# Revit family: Kombiventil 4006_M_SMART_SF_HF
name_source: partatom
category: Rohrzubehör
units: mm (PartAtom-declared; Revit-internal decimal feet)

## family parameters
Arbeitsebenenbasiert = Nein
Beim Laden mit Abzugskörper schneiden = Nein
Bemaßung runder Anschluss = Durchmesser verwenden
Gemeinsam genutzt = Nein
Immer vertikal = Ja
OmniClass-Nummer = 23.65.55.14
OmniClass-Titel = Valves for Liquid Services
Teiletyp = Unterbricht

## types (2) — shared parameters
Anwendungsgebiet = Das Kombiventil wird in allen pumpenbetriebenen Heiz- und Kühlanlagen eingesetzt.
Der Regler begrenzt automatisch den Volumenstrom im gewählten Anlagenteil auf den einmal eingestellten Wert, indem alle Druckschwankungen gemessen und ausgeregelt werden.
Somit sind keine Messungen erforderlich und die Regelung ist bei allen Betriebsbedingungen effektiv.
Das Kombiventil regelt den Volumenstrom der ventileigenen Voreinstellung auf einen konstanten Wert; die Membran regelt aufgrund des Druckes unmittelbar nach dem Regeleinsatz, sowie des Druckes davor.
Die Voreinstellung bezieht sich direkt auf den Volumenstrom; entsprechend kann die maximale Durchflussmenge bei der Montage direkt nach dem Diagramm eingestellt werden.
Somit sind z.B. Heizungsstränge, Kühlwasserkreisläufe, Deckenstrahlplatten, Kühldecken und Lufterhitzer ohne Rücksicht auf die Druckverteilung in der Anlage ohne weiteres abgleichbar.
Bauschutzkappe = Kunststoff
D03 = 19.5 mm  [stored 0.0639764 ft]
D04 = 25 mm  [stored 0.082021 ft]
D05 = 15 mm  [stored 0.0492126 ft]
D06 = 13.9 mm  [stored 0.0456037 ft]
Druckfeder = Federstahl
Gehäuse = DZR Messing CC770S
H01 = 37 mm  [stored 0.121391 ft]
H02 = 57.1 mm  [stored 0.187336 ft]
H03 = 20.5 mm  [stored 0.0672572 ft]
H04 = 9 mm  [stored 0.0295276 ft]
H05 = 5 mm  [stored 0.0164042 ft]
H06 = 48.5 mm
Hersteller = HERZ Armaturen Ges.m.b.H.
Hub = 4 mm
Impulsleitung = Kupfer Cu-DHP (CW024A)
KD01 = 17.55 mm  [stored 0.0575787 ft]
KD02 = 22 mm  [stored 0.0721785 ft]
KH01 = 10.8 mm  [stored 0.0354331 ft]
KH02 = 23 mm  [stored 0.0754593 ft]
KH03 = 2.8 mm  [stored 0.00918635 ft]
KH04 = 28.8 mm  [stored 0.0944882 ft]
KH05 = 30.5 mm  [stored 0.100066 ft]
KH06 = 32 mm  [stored 0.104987 ft]
L01 = 41 mm  [stored 0.134514 ft]
L02 = 34 mm  [stored 0.111549 ft]
LH01 = 5 mm  [stored 0.0164042 ft]
MD01 = 7.5 mm  [stored 0.0246063 ft]
MH01 = 8.5 mm  [stored 0.0278871 ft]
MH02 = 3.5 mm  [stored 0.0114829 ft]
MH03 = 9 mm  [stored 0.0295276 ft]
ML01 = 29 mm  [stored 0.0951444 ft]
ML02 = 14 mm  [stored 0.0459318 ft]
ML03 = 4 mm  [stored 0.0131234 ft]
ML04 = 17 mm  [stored 0.0557743 ft]
Max. Betriebsdruck = 2500000.0 Pa
Max. Betriebstemperatur = 130 °C
Max. Differenzdruck am Gehäuse = 600000.0 Pa
Medium = Wasserbeschaffenheit nach ÖNORM H 5195 und VDI 2035.
Die Verwendung von Ethylen- Propylenglykol ist im Mischungsverhältnis 25 -50 Vol.-[%] zulässig.
Membrane = EPDM
Membrangehäuse = Messing CW602N
Min. Betriebstemperatur (Frostschutz) = -20 °C
Min. Betriebstemperatur (reines Wasser) = 2 °C
O-Ringe = EPDM
S01 = 10 mm  [stored 0.0328084 ft]
S02 = 20.1 mm  [stored 0.0659449 ft]
S03 = 11.4 mm  [stored 0.0374016 ft]
S04 = 25 mm  [stored 0.082021 ft]
SCRNCODE = 05;04;02
SCRNSEQ = ARM;ARM_TYP="DURR";2
Stift = Edelstahl 14301
URL = www.herz-armaturen.at
VRGT = 7 mm  [stored 0.0229659 ft]
VRL01 = 30 mm  [stored 0.0984252 ft]
VRL02 = 17 mm  [stored 0.0557743 ft]
VRL03 = 11 mm  [stored 0.0360892 ft]
VRL04 = 7 mm  [stored 0.0229659 ft]
zero-valued in all types: Vorgabe-Ansicht

## type names (no varying parameters)
- SF
- HF

note: [stored X ft] marks values corroborated as IEEE doubles in the binary element streams (Revit-internal decimal feet)
